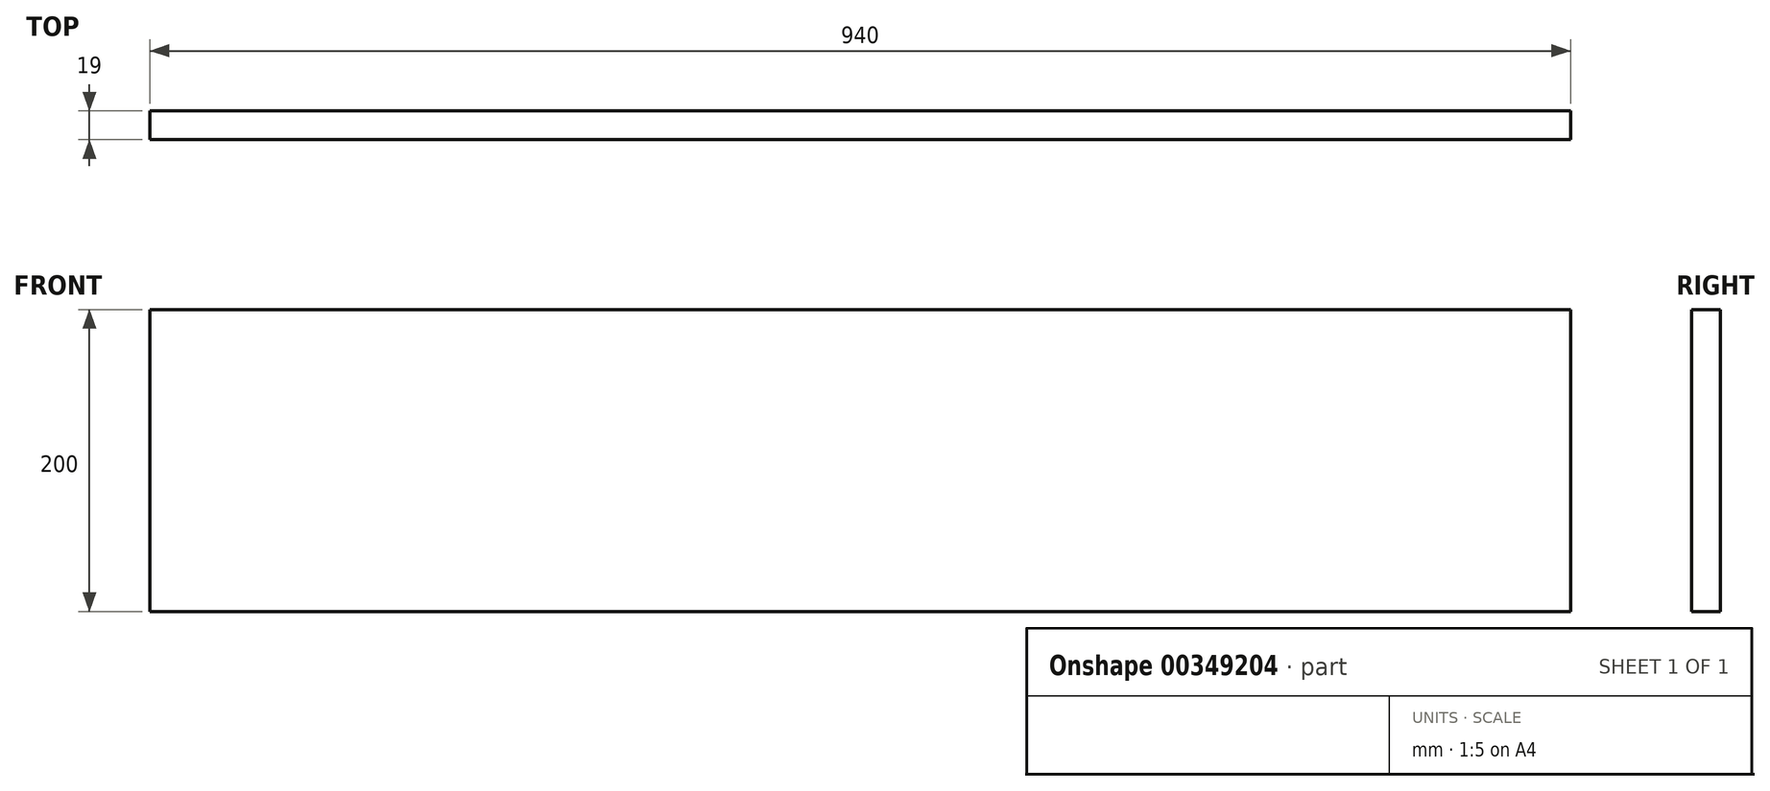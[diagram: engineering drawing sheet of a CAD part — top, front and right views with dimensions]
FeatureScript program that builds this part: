
annotation { "Feature Type Name" : "Feature", "Feature Type Description" : "" }
export const myFeature = defineFeature(function(context is Context, id is Id, definition is map)
    precondition{}
    {
        {
            var Q0;
            Q0=qCreatedBy(makeId("Front.planeOp"),FACE);
            var sketch = newSketch(context, id + "F0", { "sketchPlane" : qUnion([Q0])});
            skLineSegment(sketch, "E0.bottom", {"start": v(0, 0) * mm, "end": v(940, 0) * mm});
            skLineSegment(sketch, "E0.top", {"start": v(0, 200) * mm, "end": v(940, 200) * mm});
            skLineSegment(sketch, "E0.left", {"start": v(0, 0) * mm, "end": v(0, 200) * mm});
            skLineSegment(sketch, "E0.right", {"start": v(940, 0) * mm, "end": v(940, 200) * mm});
            skSolve(sketch);
        }
        {
            var Q0;
            Q0 = qSketchRegion(id + "F0", true);
            extrude(context, id + "F1", {"entities" : qUnion([Q0]), "depth" : 19 * mm});
        }
    });
